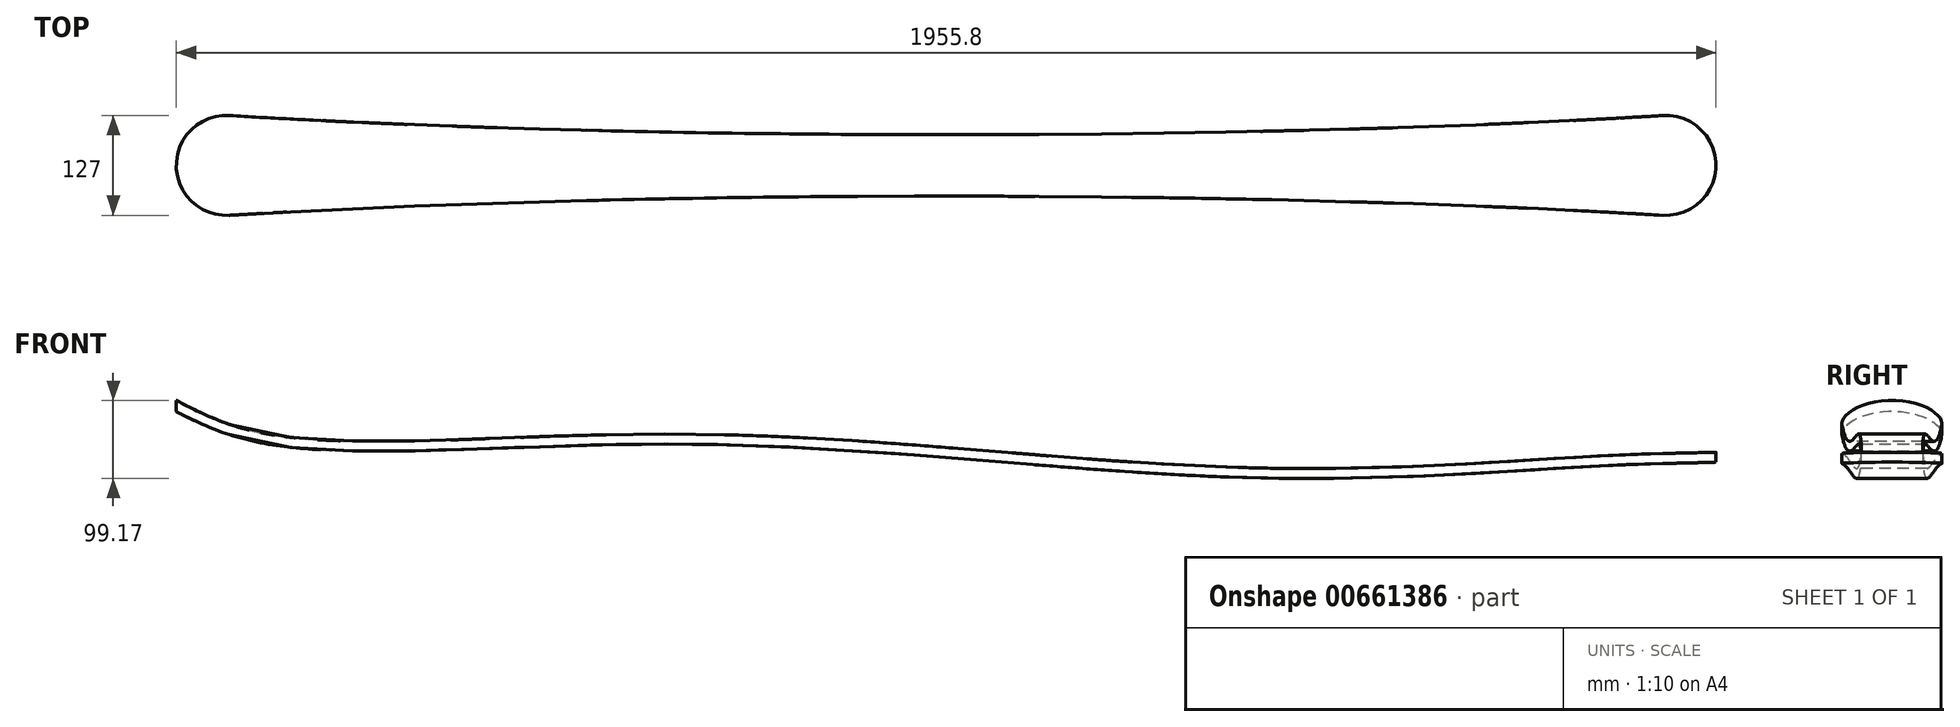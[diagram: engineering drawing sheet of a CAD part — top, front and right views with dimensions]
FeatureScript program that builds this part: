
annotation { "Feature Type Name" : "Feature", "Feature Type Description" : "" }
export const myFeature = defineFeature(function(context is Context, id is Id, definition is map)
    precondition{}
    {
        {
            var Q0;
            Q0=qCreatedBy(makeId("Top.planeOp"),FACE);
            var sketch = newSketch(context, id + "F0", { "sketchPlane" : qUnion([Q0])});
            skLineSegment(sketch, "E0", {"start": v(-914.4, 0) * mm, "end": v(914.4, 0) * mm, "construction": true});
            skEllipticalArc(sketch, "E1", {});
            skLineSegment(sketch, "E2.bottom", {"start": v(-915.06, 413.08) * mm, "end": v(-915.06, 413.08) * mm});
            skLineSegment(sketch, "E2.top", {"start": v(-915.06, 199.91) * mm, "end": v(-915.06, 199.91) * mm});
            skEllipticalArc(sketch, "E3.MirrorCS", {});
            skArc(sketch, "E4", {"start": v(-910.56, 63.38) * mm, "mid": v(-977.9, 0) * mm, "end": v(-910.56, -63.38) * mm});
            skArc(sketch, "E5", {"start": v(-910.56, -63.38) * mm, "mid": v(-850.9, 0) * mm, "end": v(-910.56, 63.38) * mm, "construction": true});
            skArc(sketch, "E6", {"start": v(910.56, 63.38) * mm, "mid": v(850.9, 0) * mm, "end": v(910.56, -63.38) * mm, "construction": true});
            skArc(sketch, "E7", {"start": v(910.56, -63.38) * mm, "mid": v(977.9, 0) * mm, "end": v(910.56, 63.38) * mm});
            const initialGuessF0  = {"E1": [0, 0.1558063245600839, 1, 0, 1.4896054020079814, 0.11678101203412063, 4.054715499518199, 5.370062461307284], "E3.MirrorCS": [0, -0.15580632456008398, 1, 0, 1.4896054020079814, 0.11678101203412063, 0.9131228458723026, 2.228469807661387]};
            skSetInitialGuess(sketch, initialGuessF0);
            skSolve(sketch);
        }
        {
            var Q0;
            Q0 = qSketchRegion(id + "F0", true);
            extrude(context, id + "F1", {"entities" : qUnion([Q0]), "depth" : 152.4 * mm, "offsetDistance" : 25.4 * mm});
        }
        {
            var Q0;
            Q0=qCreatedBy(makeId("Front.planeOp"),FACE);
            var sketch = newSketch(context, id + "F2", { "sketchPlane" : qUnion([Q0])});
            skFitSpline(sketch, "E8", {"points": [v(-1004.14, 114.8) * mm, v(-861.5, 59.59) * mm, v(-325.26, 59.57) * mm, v(400.9, 16.62) * mm, v(865.08, 33.62) * mm, v(1032.45, 40.41) * mm], "startDerivative": vector(920.7, -480.38) * mm, "endDerivative": vector(1095.75, 118.24) * mm});
            skFitSpline(sketch, "E9.0", {"points": [v(-998.26, 126.06) * mm, v(-988.56, 121) * mm, v(-974.17, 113.22) * mm, v(-954.2, 103.14) * mm, v(-938.56, 95.87) * mm, v(-921.94, 89.03) * mm, v(-904.06, 82.77) * mm, v(-887.86, 78.16) * mm, v(-873.96, 74.9) * mm, v(-864.85, 73.07) * mm, v(-857.3, 71.74) * mm, v(-849.55, 70.5) * mm, v(-839.5, 69.09) * mm, v(-826.86, 67.65) * mm, v(-809.3, 66.04) * mm, v(-786.05, 64.59) * mm, v(-756.23, 63.62) * mm, v(-724.65, 63.33) * mm, v(-680.4, 63.68) * mm, v(-621.4, 65.25) * mm, v(-545.87, 68.03) * mm, v(-479.91, 70.3) * mm, v(-425.89, 71.65) * mm, v(-384.87, 72.3) * mm, v(-350.4, 72.45) * mm, v(-322.7, 72.28) * mm, v(-294.96, 71.89) * mm, v(-260.24, 71.03) * mm, v(-218.5, 69.46) * mm, v(-176.76, 67.44) * mm, v(-121.1, 64.21) * mm, v(-51.61, 59.38) * mm, v(31.34, 52.84) * mm, v(113.62, 46.12) * mm, v(194.94, 39.78) * mm, v(261.7, 35.26) * mm, v(314.36, 32.37) * mm, v(353.45, 30.65) * mm, v(385.66, 29.63) * mm, v(411.19, 29.1) * mm, v(436.57, 28.77) * mm, v(467.98, 28.68) * mm, v(505.1, 29.06) * mm, v(541.57, 29.84) * mm, v(589.23, 31.34) * mm, v(646.77, 33.91) * mm, v(711.98, 37.6) * mm, v(762.61, 40.74) * mm, v(800.59, 43.02) * mm, v(827.73, 44.56) * mm, v(849.18, 45.65) * mm, v(865.6, 46.36) * mm, v(877.52, 46.8) * mm, v(889.07, 47.19) * mm, v(904, 47.62) * mm, v(921.82, 48.04) * mm, v(942.02, 48.46) * mm, v(967.6, 49.06) * mm, v(997.44, 50.12) * mm, v(1019.94, 51.84) * mm, v(1031.08, 53.04) * mm]});
            skLineSegment(sketch, "E10", {"start": v(-998.26, 126.06) * mm, "end": v(-1004.14, 114.8) * mm});
            skLineSegment(sketch, "E11", {"start": v(1026.34, 52.55) * mm, "end": v(1032.45, 40.41) * mm});
            skSolve(sketch);
        }
        {
            var Q0;
            Q0 = qSketchRegion(id + "F2", true);
            extrude(context, id + "F3", {"entities" : qUnion([Q0]), "operationType" : NewBodyOperationType.INTERSECT, "depth" : 254 * mm, "offsetDistance" : 25.4 * mm, "hasSecondDirection" : true, "secondDirectionBound" : BoundingType.THROUGH_ALL, "secondDirectionOppositeDirection" : false, "secondDirectionDepth" : 25.4 * mm, "symmetric" : true});
        }
    });
